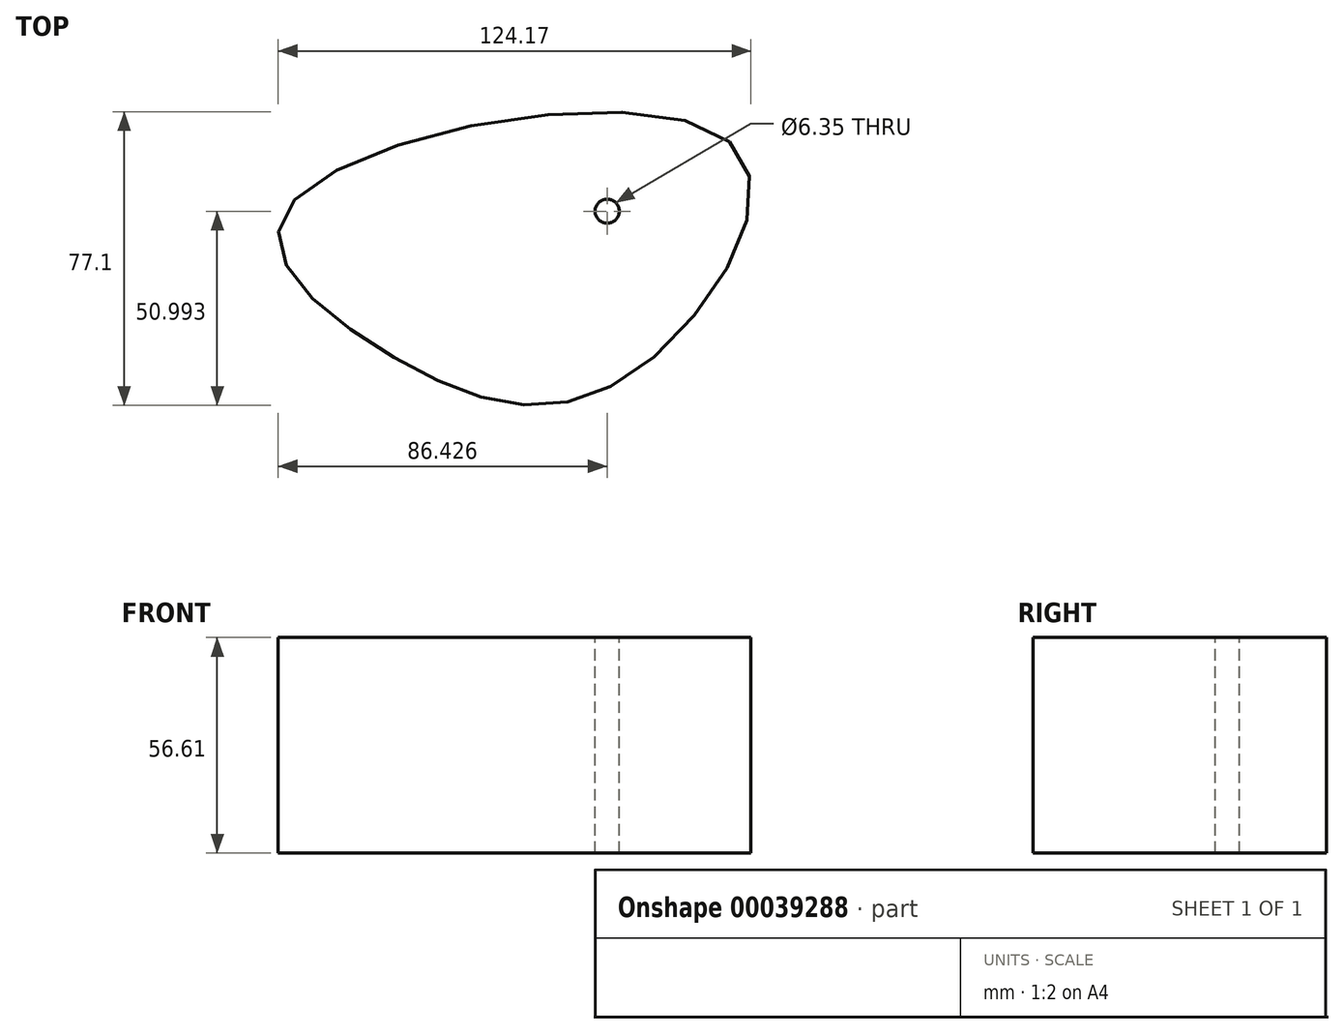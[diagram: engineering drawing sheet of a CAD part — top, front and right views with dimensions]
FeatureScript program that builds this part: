
annotation { "Feature Type Name" : "Feature", "Feature Type Description" : "" }
export const myFeature = defineFeature(function(context is Context, id is Id, definition is map)
    precondition{}
    {
        {
            var Q0;
            Q0=qCreatedBy(makeId("Top.planeOp"),FACE);
            var sketch = newSketch(context, id + "F0", { "sketchPlane" : qUnion([Q0])});
            skFitSpline(sketch, "E0", {"points": [v(-76.2, -11.15) * mm, v(-104.26, 27.95) * mm, v(12.78, 44.74) * mm, v(-16.04, -16.92) * mm, v(-76.2, -11.15) * mm]});
            skSolve(sketch);
        }
        {
            var Q0;
            Q0=makeQuery(id+"F0.imprint","IMPRINT",FACE,{"disambiguationData":[TD([[makeQuery(id+"F0.imprint","IMPRINT",EDGE,{"derivedFrom":sQuery(id+"F0.wireOp",EDGE,"E0")}),-1.0]])]});
            extrude(context, id + "F1", {"entities" : qUnion([Q0]), "depth" : 56.6 * mm});
        }
        {
            var Q0;
            Q0=makeQuery(id+"F1.opExtrude","CAP_FACE",FACE,{"disambiguationData":[OSD([sQuery(id+"F0.wireOp",EDGE,"E0")])],"isStart":false});
            var sketch = newSketch(context, id + "F2", { "sketchPlane" : qUnion([Q0])});
            skFitSpline(sketch, "E1", {"points": [v(-39.51, 21.11) * mm, v(-56.53, 31.03) * mm, v(-47.64, 9.51) * mm, v(-39.51, 21.11) * mm]});
            skPoint(sketch, "E2", {"position": v(-20.2, 27.3) * mm});
            skPoint(sketch, "E3", {"position": v(-20.86, 23.82) * mm});
            skSolve(sketch);
        }
        {
            var Q0;
            Q0=sQuery(id+"F2.wireOp",EDGE,"E1");
            extrude(context, id + "F3", {"bodyType" : ToolBodyType.SURFACE, "surfaceEntities" : qUnion([Q0]), "oppositeDirection" : true, "depth" : 22.87 * mm});
        }
        {
            var Q0;
            Q0=sQuery(id+"F2.wireOp",VERTEX,"E2");
            var Q1;
            Q1=makeQuery(id+"F1.opExtrude","SWEPT_BODY",BODY,{"disambiguationData":[OSD([sQuery(id+"F0.wireOp",EDGE,"E0")])]});
            hole(context, id + "F4", {"style" : HoleStyle.SIMPLE, "holeDiameter" : 6.35 * mm, "endStyle" : HoleEndStyle.THROUGH, "locations" : qUnion([Q0]), "scope" : qUnion([Q1])});
        }
    });
